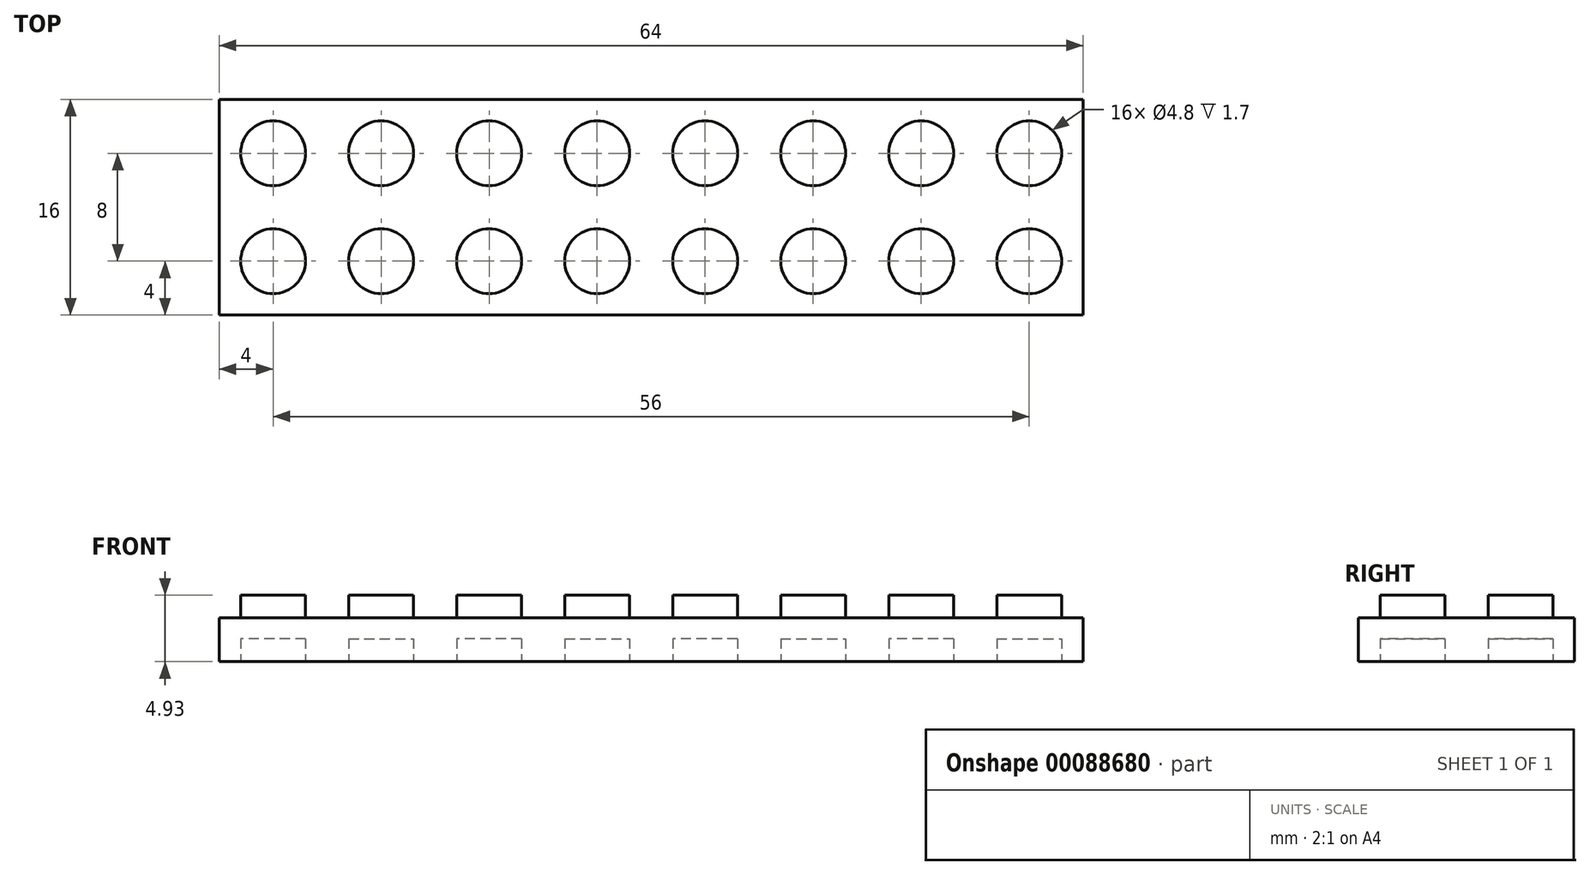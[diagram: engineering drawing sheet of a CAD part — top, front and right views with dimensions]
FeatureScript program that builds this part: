
annotation { "Feature Type Name" : "Feature", "Feature Type Description" : "" }
export const myFeature = defineFeature(function(context is Context, id is Id, definition is map)
    precondition{}
    {
        {
            var Q0;
            Q0=qCreatedBy(makeId("Front.planeOp"),FACE);
            var sketch = newSketch(context, id + "F0", { "sketchPlane" : qUnion([Q0])});
            skLineSegment(sketch, "E0.bottom", {"start": v(-4, 3.23) * mm, "end": v(-2.4, 3.23) * mm});
            skLineSegment(sketch, "E0.top", {"start": v(-4, 0) * mm, "end": v(4, 0) * mm});
            skLineSegment(sketch, "E0.left", {"start": v(-4, 3.23) * mm, "end": v(-4, 0) * mm});
            skLineSegment(sketch, "E0.right", {"start": v(4, 3.23) * mm, "end": v(4, 0) * mm});
            skLineSegment(sketch, "E1.top", {"start": v(-2.4, 4.93) * mm, "end": v(2.4, 4.93) * mm});
            skLineSegment(sketch, "E1.left", {"start": v(-2.4, 3.23) * mm, "end": v(-2.4, 4.93) * mm});
            skLineSegment(sketch, "E1.right", {"start": v(2.4, 3.23) * mm, "end": v(2.4, 4.93) * mm});
            skLineSegment(sketch, "E2", {"start": v(0, 0) * mm, "end": v(0, 24.04) * mm, "construction": true});
            skLineSegment(sketch, "E3.trimOffspring", {"start": v(2.4, 3.23) * mm, "end": v(4, 3.23) * mm});
            skSolve(sketch);
        }
        {
            var Q0;
            Q0=makeQuery(id+"F0.imprint","IMPRINT",FACE,{"disambiguationData":[TD([[makeQuery(id+"F0.imprint","IMPRINT",EDGE,{"derivedFrom":sQuery(id+"F0.wireOp",EDGE,"E0.bottom")}),-1.0]])]});
            extrude(context, id + "F1", {"entities" : qUnion([Q0]), "depth" : 8 * mm});
        }
        {
            var Q0;
            Q0=qCreatedBy(makeId("Top.planeOp"),FACE);
            var Q1;
            Q1=makeQuery(id+"F1.opExtrude","CAP_VERTEX",VERTEX,{"disambiguationData":[OSD([sQuery(id+"F0.wireOp",EDGE,"E1.top"),sQuery(id+"F0.wireOp",EDGE,"E1.right")])],"isStart":true});
            cPlane(context, id + "F2", {"entities" : qUnion([Q0, Q1]), "cplaneType" : CPlaneType.PLANE_POINT, "offset" : 152.4 * mm, "width" : 152.4 * mm, "height" : 152.4 * mm});
        }
        {
            var Q0;
            Q0=qCreatedBy(id+"F2.planeOp",FACE);
            var sketch = newSketch(context, id + "F3", { "sketchPlane" : qUnion([Q0])});
            skLineSegment(sketch, "E4.0", {"start": v(-4, -8) * mm, "end": v(-4, 0) * mm});
            skLineSegment(sketch, "E5.0", {"start": v(4, -8) * mm, "end": v(4, 0) * mm});
            skLineSegment(sketch, "E6", {"start": v(-4, 0) * mm, "end": v(4, 0) * mm});
            skLineSegment(sketch, "E7", {"start": v(-4, -8) * mm, "end": v(4, -8) * mm});
            skLineSegment(sketch, "E8", {"start": v(-4, 0) * mm, "end": v(4, -8) * mm, "construction": true});
            skLineSegment(sketch, "E9", {"start": v(-4, -8) * mm, "end": v(4, 0) * mm, "construction": true});
            skCircle(sketch, "E10", {"center": v(0, -4) * mm, "radius": 2.4 * mm});
            skSolve(sketch);
        }
        {
            var Q0;
            Q0=qSketchRegion(id+"F3",true);
            var Q1;
            Q1=makeQuery(id+"F1.opExtrude","SWEPT_FACE",FACE,{"disambiguationData":[OSD([sQuery(id+"F0.wireOp",EDGE,"E0.bottom")])]});
            extrude(context, id + "F4", {"entities" : qUnion([Q0]), "operationType" : NewBodyOperationType.REMOVE, "endBound" : BoundingType.UP_TO_SURFACE, "oppositeDirection" : true, "endBoundEntityFace" : qUnion([Q1]), "depth" : 25.4 * mm});
        }
        {
            var Q0;
            Q0=qCreatedBy(makeId("Top.planeOp"),FACE);
            var sketch = newSketch(context, id + "F5", { "sketchPlane" : qUnion([Q0])});
            skCircle(sketch, "E11.0", {"center": v(0, -4) * mm, "radius": 2.4 * mm});
            skSolve(sketch);
        }
        {
            var Q0;
            Q0=makeQuery(id+"F5.imprint","IMPRINT",FACE,{"disambiguationData":[TD([[makeQuery(id+"F5.imprint","IMPRINT",EDGE,{"derivedFrom":sQuery(id+"F5.wireOp",EDGE,"E11.0")}),1.0]])]});
            extrude(context, id + "F6", {"entities" : qUnion([Q0]), "operationType" : NewBodyOperationType.REMOVE, "depth" : 1.7 * mm});
        }
        {
            var Q0;
            Q0=qCreatedBy(makeId("Right.planeOp"),FACE);
            var Q1;
            Q1=makeQuery(id+"F1.opExtrude","CAP_VERTEX",VERTEX,{"disambiguationData":[OSD([sQuery(id+"F0.wireOp",EDGE,"E0.right"),sQuery(id+"F0.wireOp",EDGE,"E3.trimOffspring")])],"isStart":false});
            cPlane(context, id + "F7", {"entities" : qUnion([Q0, Q1]), "cplaneType" : CPlaneType.PLANE_POINT, "offset" : 152.4 * mm, "width" : 152.4 * mm, "height" : 152.4 * mm});
        }
        {
            var Q0;
            Q0=makeQuery(id+"F1.opExtrude","SWEPT_BODY",BODY,{"disambiguationData":[OSD([sQuery(id+"F0.wireOp",EDGE,"E0.bottom"),sQuery(id+"F0.wireOp",EDGE,"E0.top"),sQuery(id+"F0.wireOp",EDGE,"E0.left"),sQuery(id+"F0.wireOp",EDGE,"E0.right"),sQuery(id+"F0.wireOp",EDGE,"E1.top"),sQuery(id+"F0.wireOp",EDGE,"E1.left"),sQuery(id+"F0.wireOp",EDGE,"E1.right"),sQuery(id+"F0.wireOp",EDGE,"E3.trimOffspring")])]});
            var Q1;
            Q1=qCreatedBy(id+"F7.planeOp",FACE);
            mirror(context, id + "F8", {"operationType" : NewBodyOperationType.ADD, "entities" : qUnion([Q0]), "mirrorPlane" : qUnion([Q1])});
        }
        {
            var Q0;
            Q0=makeQuery(id+"F1.opExtrude","SWEPT_BODY",BODY,{"disambiguationData":[OSD([sQuery(id+"F0.wireOp",EDGE,"E0.bottom"),sQuery(id+"F0.wireOp",EDGE,"E0.top"),sQuery(id+"F0.wireOp",EDGE,"E0.left"),sQuery(id+"F0.wireOp",EDGE,"E0.right"),sQuery(id+"F0.wireOp",EDGE,"E1.top"),sQuery(id+"F0.wireOp",EDGE,"E1.left"),sQuery(id+"F0.wireOp",EDGE,"E1.right"),sQuery(id+"F0.wireOp",EDGE,"E3.trimOffspring")])]});
            var Q1;
            Q1=qCreatedBy(makeId("Front.planeOp"),FACE);
            mirror(context, id + "F9", {"operationType" : NewBodyOperationType.ADD, "entities" : qUnion([Q0]), "mirrorPlane" : qUnion([Q1])});
        }
        {
            var Q0;
            Q0=qCreatedBy(id+"F7.planeOp",FACE);
            var Q1;
            Q1=makeQuery(id+"F9.opPattern","COPY",VERTEX,{"derivedFrom":makeQuery(id+"F8.opPattern","COPY",VERTEX,{"derivedFrom":makeQuery(id+"F1.opExtrude","CAP_VERTEX",VERTEX,{"disambiguationData":[OSD([sQuery(id+"F0.wireOp",EDGE,"E0.bottom"),sQuery(id+"F0.wireOp",EDGE,"E0.left")])],"isStart":false}),"instanceName":"1"}),"instanceName":"1"});
            cPlane(context, id + "F10", {"entities" : qUnion([Q0, Q1]), "cplaneType" : CPlaneType.PLANE_POINT, "offset" : 152.4 * mm, "width" : 152.4 * mm, "height" : 152.4 * mm});
        }
        {
            var Q0;
            Q0=makeQuery(id+"F1.opExtrude","SWEPT_BODY",BODY,{"disambiguationData":[OSD([sQuery(id+"F0.wireOp",EDGE,"E0.bottom"),sQuery(id+"F0.wireOp",EDGE,"E0.top"),sQuery(id+"F0.wireOp",EDGE,"E0.left"),sQuery(id+"F0.wireOp",EDGE,"E0.right"),sQuery(id+"F0.wireOp",EDGE,"E1.top"),sQuery(id+"F0.wireOp",EDGE,"E1.left"),sQuery(id+"F0.wireOp",EDGE,"E1.right"),sQuery(id+"F0.wireOp",EDGE,"E3.trimOffspring")])]});
            var Q1;
            Q1=qCreatedBy(id+"F10.planeOp",FACE);
            mirror(context, id + "F11", {"operationType" : NewBodyOperationType.ADD, "entities" : qUnion([Q0]), "mirrorPlane" : qUnion([Q1])});
        }
        {
            var Q0;
            Q0=makeQuery(id+"F1.opExtrude","SWEPT_BODY",BODY,{"disambiguationData":[OSD([sQuery(id+"F0.wireOp",EDGE,"E0.bottom"),sQuery(id+"F0.wireOp",EDGE,"E0.top"),sQuery(id+"F0.wireOp",EDGE,"E0.left"),sQuery(id+"F0.wireOp",EDGE,"E0.right"),sQuery(id+"F0.wireOp",EDGE,"E1.top"),sQuery(id+"F0.wireOp",EDGE,"E1.left"),sQuery(id+"F0.wireOp",EDGE,"E1.right"),sQuery(id+"F0.wireOp",EDGE,"E3.trimOffspring")])]});
            var Q1;
            {var subQ0=makeQuery(id+"F1.opExtrude","SWEPT_FACE",FACE,{"disambiguationData":[OSD([sQuery(id+"F0.wireOp",EDGE,"E0.left")])]});Q1=makeQuery(id+"F11.opPattern","COPY",FACE,{"derivedFrom":makeQuery(id+"F9.boolean.opBoolean","MERGE",FACE,{"derivedFrom":[subQ0,makeQuery(id+"F9.opPattern","COPY",FACE,{"derivedFrom":subQ0,"instanceName":"1"})]}),"instanceName":"1"});}
            mirror(context, id + "F12", {"operationType" : NewBodyOperationType.ADD, "entities" : qUnion([Q0]), "mirrorPlane" : qUnion([Q1])});
        }
    });
